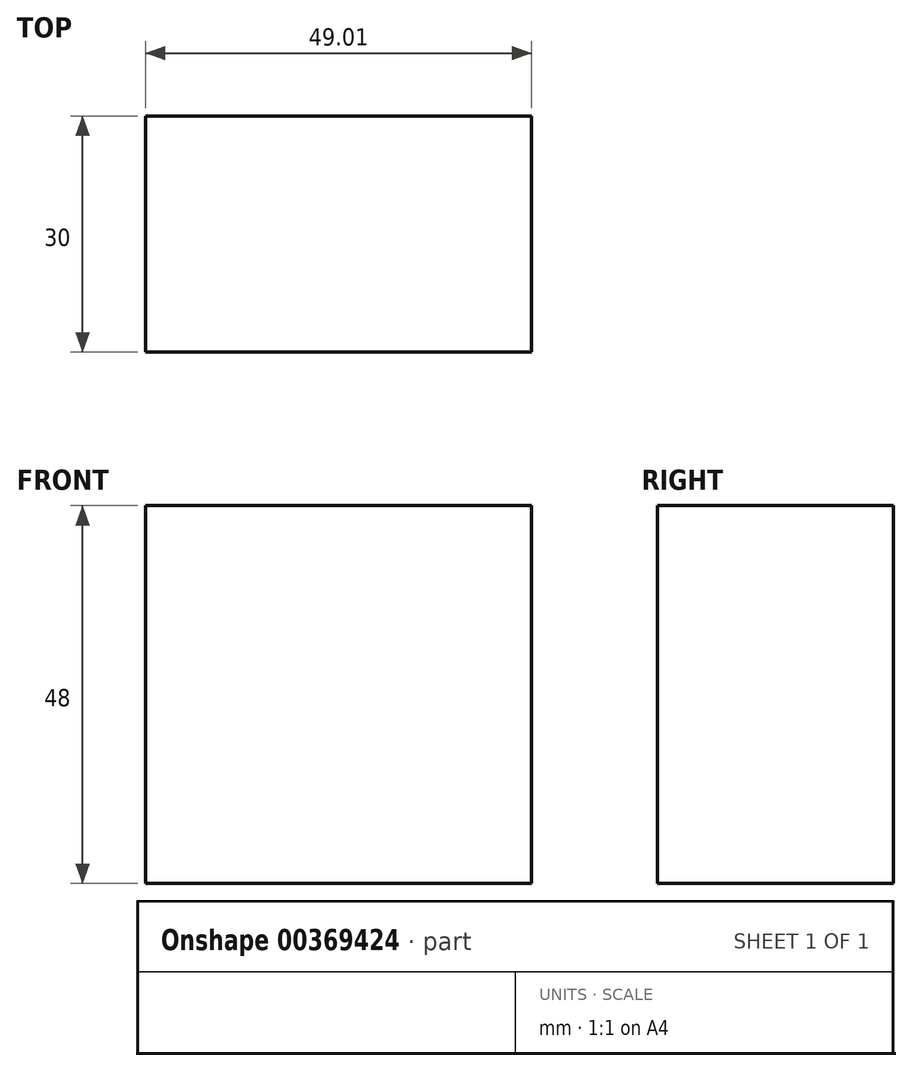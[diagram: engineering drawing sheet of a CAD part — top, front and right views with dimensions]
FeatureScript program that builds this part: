
annotation { "Feature Type Name" : "Feature", "Feature Type Description" : "" }
export const myFeature = defineFeature(function(context is Context, id is Id, definition is map)
    precondition{}
    {
        {
            var Q0;
            Q0=qCreatedBy(makeId("Front.planeOp"),FACE);
            var sketch = newSketch(context, id + "F0", { "sketchPlane" : qUnion([Q0])});
            skLineSegment(sketch, "E0.bottom", {"start": v(0, 0) * mm, "end": v(49.01, 0) * mm});
            skLineSegment(sketch, "E0.top", {"start": v(0, 48) * mm, "end": v(49.01, 48) * mm});
            skLineSegment(sketch, "E0.left", {"start": v(0, 0) * mm, "end": v(0, 48) * mm});
            skLineSegment(sketch, "E0.right", {"start": v(49.01, 0) * mm, "end": v(49.01, 48) * mm});
            skSolve(sketch);
        }
        {
            var Q0;
            Q0=makeQuery(id+"F0.imprint","IMPRINT",FACE,{"disambiguationData":[TD([[makeQuery(id+"F0.imprint","IMPRINT",EDGE,{"derivedFrom":sQuery(id+"F0.wireOp",EDGE,"E0.bottom")}),1.0]])]});
            extrude(context, id + "F1", {"entities" : qUnion([Q0]), "depth" : 30 * mm});
        }
    });
